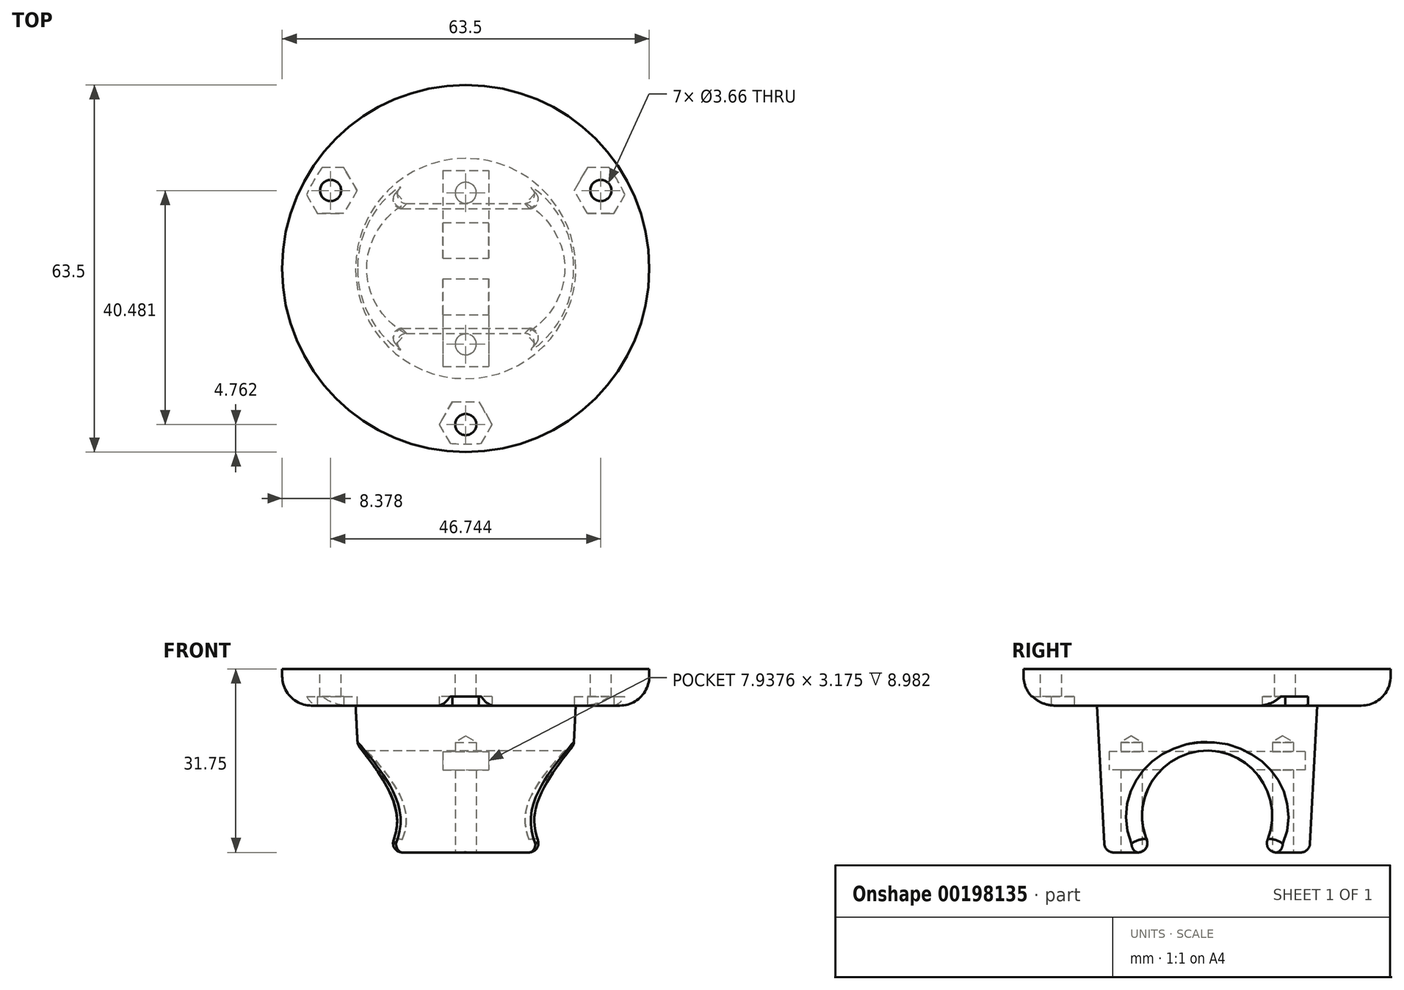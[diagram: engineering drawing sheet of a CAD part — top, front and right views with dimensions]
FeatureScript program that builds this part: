
annotation { "Feature Type Name" : "Feature", "Feature Type Description" : "" }
export const myFeature = defineFeature(function(context is Context, id is Id, definition is map)
    precondition{}
    {
        {
            var Q0;
            Q0=qCreatedBy(makeId("Top.planeOp"),FACE);
            var sketch = newSketch(context, id + "F0", { "sketchPlane" : qUnion([Q0])});
            skCircle(sketch, "E0", {"center": v(0, 0) * mm, "radius": 31.75 * mm});
            skCircle(sketch, "E1", {"center": v(0, 0) * mm, "radius": 26.99 * mm, "construction": true});
            skPoint(sketch, "E2", {"position": v(0, -26.99) * mm});
            skPoint(sketch, "E3.1.0", {"position": v(23.37, 13.5) * mm});
            skPoint(sketch, "E3.2.0", {"position": v(-23.37, 13.5) * mm});
            skSolve(sketch);
        }
        {
            var Q0;
            Q0 = qSketchRegion(id + "F0", true);
            extrude(context, id + "F1", {"entities" : qUnion([Q0]), "oppositeDirection" : true, "depth" : 6.35 * mm});
        }
        {
            var Q0;
            Q0=sQuery(id+"F0.wireOp",VERTEX,"E3.2.0");
            var Q1;
            Q1=sQuery(id+"F0.wireOp",VERTEX,"E3.1.0");
            var Q2;
            Q2=sQuery(id+"F0.wireOp",VERTEX,"E2");
            var Q3;
            Q3=makeQuery(id+"F1.opExtrude","SWEPT_BODY",BODY,{"disambiguationData":[OSD([sQuery(id+"F0.wireOp",EDGE,"E0")])]});
            hole(context, id + "F2", {"style" : HoleStyle.SIMPLE, "endStyle" : HoleEndStyle.THROUGH, "standardTappedOrClearance" : lookupTablePath({ "standard" : "ANSI", "fit" : "Close", "size" : "#6", "type" : "Clearance" }), "standardBlindInLast" : lookupTablePath({ "fit" : "Close", "standard" : "ANSI", "size" : "#6", "type" : "Clearance" }), "holeDiameter" : 3.66 * mm, "startFromSketch" : true, "locations" : qUnion([Q0, Q1, Q2]), "scope" : qUnion([Q3]), "isTappedThrough" : true});
        }
        {
            var Q0;
            Q0=makeQuery(id+"F1.opExtrude","CAP_FACE",FACE,{"disambiguationData":[OSD([sQuery(id+"F0.wireOp",EDGE,"E0")])],"isStart":false});
            var sketch = newSketch(context, id + "F3", { "sketchPlane" : qUnion([Q0])});
            skCircle(sketch, "E4", {"center": v(0, 0) * mm, "radius": 19.05 * mm});
            skSolve(sketch);
        }
        {
            var Q0;
            Q0 = qSketchRegion(id + "F3", true);
            extrude(context, id + "F4", {"entities" : qUnion([Q0]), "operationType" : NewBodyOperationType.ADD, "depth" : 25.4 * mm, "hasDraft" : true, "draftAngle" : 3 * degree, "draftPullDirection" : true});
        }
        {
            var Q0;
            Q0=makeQuery(id+"F4.opExtrude","CAP_EDGE",EDGE,{"disambiguationData":[OSD([sQuery(id+"F3.wireOp",EDGE,"E4")])],"isStart":true});
            var Q1;
            Q1=makeQuery(id+"F1.opExtrude","CAP_EDGE",EDGE,{"disambiguationData":[OSD([sQuery(id+"F0.wireOp",EDGE,"E0")])],"isStart":false});
            fillet(context, id + "F5", {"entities" : qUnion([Q0, Q1]), "radius" : 5.08 * mm, "tangentPropagation" : true, "allowEdgeOverflow" : false});
        }
        {
            var Q0;
            Q0=qCreatedBy(makeId("Right.planeOp"),FACE);
            var sketch = newSketch(context, id + "F6", { "sketchPlane" : qUnion([Q0])});
            skCircle(sketch, "E5", {"center": v(0, -25.4) * mm, "radius": 11.25 * mm});
            skSolve(sketch);
        }
        {
            var Q0;
            Q0 = qSketchRegion(id + "F6", true);
            extrude(context, id + "F7", {"entities" : qUnion([Q0]), "operationType" : NewBodyOperationType.REMOVE, "endBound" : BoundingType.SYMMETRIC, "oppositeDirection" : true, "depth" : 50.8 * mm});
        }
        {
            var Q0;
            Q0=makeQuery(id+"F7.boolean.opBoolean","SPLIT",FACE,{"disambiguationData":[OD(0.0)],"derivedFrom":makeQuery(id+"F4.opExtrude","CAP_FACE",FACE,{"disambiguationData":[OSD([sQuery(id+"F3.wireOp",EDGE,"E4")])],"isStart":false})});
            var sketch = newSketch(context, id + "F8", { "sketchPlane" : qUnion([Q0])});
            skPoint(sketch, "E6", {"position": v(0, 13.1) * mm});
            skPoint(sketch, "E7", {"position": v(0, -13.1) * mm});
            skSolve(sketch);
        }
        {
            var Q0;
            Q0=sQuery(id+"F8.wireOp",VERTEX,"E6");
            var Q1;
            Q1=sQuery(id+"F8.wireOp",VERTEX,"E7");
            var Q2;
            Q2=makeQuery(id+"F1.opExtrude","SWEPT_BODY",BODY,{"disambiguationData":[OSD([sQuery(id+"F0.wireOp",EDGE,"E0")])]});
            hole(context, id + "F9", {"style" : HoleStyle.SIMPLE, "endStyle" : HoleEndStyle.BLIND, "standardTappedOrClearance" : lookupTablePath({ "standard" : "ANSI", "fit" : "Close", "size" : "#6", "type" : "Clearance" }), "standardBlindInLast" : lookupTablePath({ "fit" : "Close", "standard" : "ANSI", "size" : "#6", "type" : "Clearance" }), "holeDiameter" : 3.66 * mm, "holeDepth" : 19.05 * mm, "startFromSketch" : true, "locations" : qUnion([Q0, Q1]), "scope" : qUnion([Q2])});
        }
        {
            var Q0;
            Q0=qCreatedBy(makeId("Front.planeOp"),FACE);
            var sketch = newSketch(context, id + "F10", { "sketchPlane" : qUnion([Q0])});
            skLineSegment(sketch, "E8.bottom", {"start": v(-3.97, -14.29) * mm, "end": v(3.97, -14.29) * mm});
            skLineSegment(sketch, "E8.top", {"start": v(-3.97, -17.46) * mm, "end": v(3.97, -17.46) * mm});
            skLineSegment(sketch, "E8.left", {"start": v(-3.97, -14.29) * mm, "end": v(-3.97, -17.46) * mm});
            skLineSegment(sketch, "E8.right", {"start": v(3.97, -14.29) * mm, "end": v(3.97, -17.46) * mm});
            skLineSegment(sketch, "E9", {"start": v(0, -14.29) * mm, "end": v(0, -17.46) * mm, "construction": true});
            skSolve(sketch);
        }
        {
            var Q0;
            Q0 = qSketchRegion(id + "F10", true);
            extrude(context, id + "F11", {"entities" : qUnion([Q0]), "operationType" : NewBodyOperationType.REMOVE, "endBound" : BoundingType.SYMMETRIC, "oppositeDirection" : true, "depth" : 33.9 * mm});
        }
        {
            var Q0;
            Q0=makeQuery(id+"F1.opExtrude","CAP_FACE",FACE,{"disambiguationData":[OSD([sQuery(id+"F0.wireOp",EDGE,"E0")])],"isStart":false});
            var sketch = newSketch(context, id + "F12", { "sketchPlane" : qUnion([Q0])});
            skCircle(sketch, "E10.cCircle", {"center": v(0, 26.99) * mm, "radius": 3.97 * mm, "construction": true});
            skLineSegment(sketch, "E10.0", {"start": v(-2.3, 30.96) * mm, "end": v(2.3, 30.96) * mm});
            skLineSegment(sketch, "E10.1", {"start": v(2.3, 30.96) * mm, "end": v(4.58, 26.99) * mm});
            skLineSegment(sketch, "E10.2", {"start": v(4.58, 26.99) * mm, "end": v(2.3, 23.02) * mm});
            skLineSegment(sketch, "E10.3", {"start": v(2.3, 23.02) * mm, "end": v(-2.3, 23.02) * mm});
            skLineSegment(sketch, "E10.4", {"start": v(-2.3, 23.02) * mm, "end": v(-4.58, 26.99) * mm});
            skLineSegment(sketch, "E10.5", {"start": v(-4.58, 26.99) * mm, "end": v(-2.3, 30.96) * mm});
            skPoint(sketch, "E10.0.midPoint", {"position": v(0, 30.96) * mm});
            skPoint(sketch, "E11.1.0", {"position": v(-26.8, -15.48) * mm});
            skLineSegment(sketch, "E11.1.1", {"start": v(-21.08, -17.46) * mm, "end": v(-25.66, -17.46) * mm});
            skLineSegment(sketch, "E11.1.2", {"start": v(-21.08, -9.52) * mm, "end": v(-18.79, -13.5) * mm});
            skLineSegment(sketch, "E11.1.3", {"start": v(-18.79, -13.5) * mm, "end": v(-21.08, -17.46) * mm});
            skCircle(sketch, "E11.1.4", {"center": v(-23.37, -13.5) * mm, "radius": 3.97 * mm, "construction": true});
            skLineSegment(sketch, "E11.1.5", {"start": v(-25.66, -17.46) * mm, "end": v(-27.95, -13.5) * mm});
            skLineSegment(sketch, "E11.1.6", {"start": v(-27.95, -13.5) * mm, "end": v(-25.66, -9.52) * mm});
            skLineSegment(sketch, "E11.1.7", {"start": v(-25.66, -9.52) * mm, "end": v(-21.08, -9.52) * mm});
            skPoint(sketch, "E11.2.0", {"position": v(26.8, -15.48) * mm});
            skLineSegment(sketch, "E11.2.1", {"start": v(25.66, -9.53) * mm, "end": v(27.95, -13.5) * mm});
            skLineSegment(sketch, "E11.2.2", {"start": v(18.79, -13.5) * mm, "end": v(21.08, -9.53) * mm});
            skLineSegment(sketch, "E11.2.3", {"start": v(21.08, -9.53) * mm, "end": v(25.66, -9.53) * mm});
            skCircle(sketch, "E11.2.4", {"center": v(23.37, -13.5) * mm, "radius": 3.97 * mm, "construction": true});
            skLineSegment(sketch, "E11.2.5", {"start": v(27.95, -13.5) * mm, "end": v(25.66, -17.46) * mm});
            skLineSegment(sketch, "E11.2.6", {"start": v(25.66, -17.46) * mm, "end": v(21.08, -17.46) * mm});
            skLineSegment(sketch, "E11.2.7", {"start": v(21.08, -17.46) * mm, "end": v(18.79, -13.5) * mm});
            skPoint(sketch, "E11.center", {"position": v(0, 0) * mm});
            skSolve(sketch);
        }
        {
            var Q0;
            Q0 = qSketchRegion(id + "F12", true);
            extrude(context, id + "F13", {"entities" : qUnion([Q0]), "operationType" : NewBodyOperationType.REMOVE, "endBound" : BoundingType.SYMMETRIC, "oppositeDirection" : true, "depth" : 3.17 * mm});
        }
        {
            var Q0;
            Q0=makeQuery(id+"F7.boolean.opBoolean","INTERSECT",EDGE,{"disambiguationData":[OD(0.0)],"derivedFrom":[makeQuery(id+"F4.opExtrude","CAP_FACE",FACE,{"disambiguationData":[OSD([sQuery(id+"F3.wireOp",EDGE,"E4")])],"isStart":false}),makeQuery(id+"F7.opExtrude","SWEPT_FACE",FACE,{"disambiguationData":[OSD([sQuery(id+"F6.wireOp",EDGE,"E5")])]})]});
            var Q1;
            Q1=makeQuery(id+"F7.boolean.opBoolean","INTERSECT",EDGE,{"disambiguationData":[OD(0.0)],"derivedFrom":[makeQuery(id+"F4.opExtrude","SWEPT_FACE",FACE,{"disambiguationData":[OSD([sQuery(id+"F3.wireOp",EDGE,"E4")])]}),makeQuery(id+"F7.opExtrude","SWEPT_FACE",FACE,{"disambiguationData":[OSD([sQuery(id+"F6.wireOp",EDGE,"E5")])]})]});
            var Q2;
            Q2=makeQuery(id+"F7.boolean.opBoolean","INTERSECT",EDGE,{"disambiguationData":[OD(1.0)],"derivedFrom":[makeQuery(id+"F4.opExtrude","CAP_FACE",FACE,{"disambiguationData":[OSD([sQuery(id+"F3.wireOp",EDGE,"E4")])],"isStart":false}),makeQuery(id+"F7.opExtrude","SWEPT_FACE",FACE,{"disambiguationData":[OSD([sQuery(id+"F6.wireOp",EDGE,"E5")])]})]});
            var Q3;
            Q3=makeQuery(id+"F7.boolean.opBoolean","INTERSECT",EDGE,{"disambiguationData":[OD(1.0)],"derivedFrom":[makeQuery(id+"F4.opExtrude","SWEPT_FACE",FACE,{"disambiguationData":[OSD([sQuery(id+"F3.wireOp",EDGE,"E4")])]}),makeQuery(id+"F7.opExtrude","SWEPT_FACE",FACE,{"disambiguationData":[OSD([sQuery(id+"F6.wireOp",EDGE,"E5")])]})]});
            var Q4;
            Q4=makeQuery(id+"F7.boolean.opBoolean","SPLIT",EDGE,{"disambiguationData":[OD(1.0)],"derivedFrom":makeQuery(id+"F4.opExtrude","CAP_EDGE",EDGE,{"disambiguationData":[OSD([sQuery(id+"F3.wireOp",EDGE,"E4")])],"isStart":false})});
            var Q5;
            Q5=makeQuery(id+"F7.boolean.opBoolean","SPLIT",EDGE,{"disambiguationData":[OD(0.0)],"derivedFrom":makeQuery(id+"F4.opExtrude","CAP_EDGE",EDGE,{"disambiguationData":[OSD([sQuery(id+"F3.wireOp",EDGE,"E4")])],"isStart":false})});
            fillet(context, id + "F14", {"entities" : qUnion([Q0, Q1, Q2, Q3, Q4, Q5]), "radius" : 1.59 * mm, "tangentPropagation" : true, "allowEdgeOverflow" : false});
        }
    });
